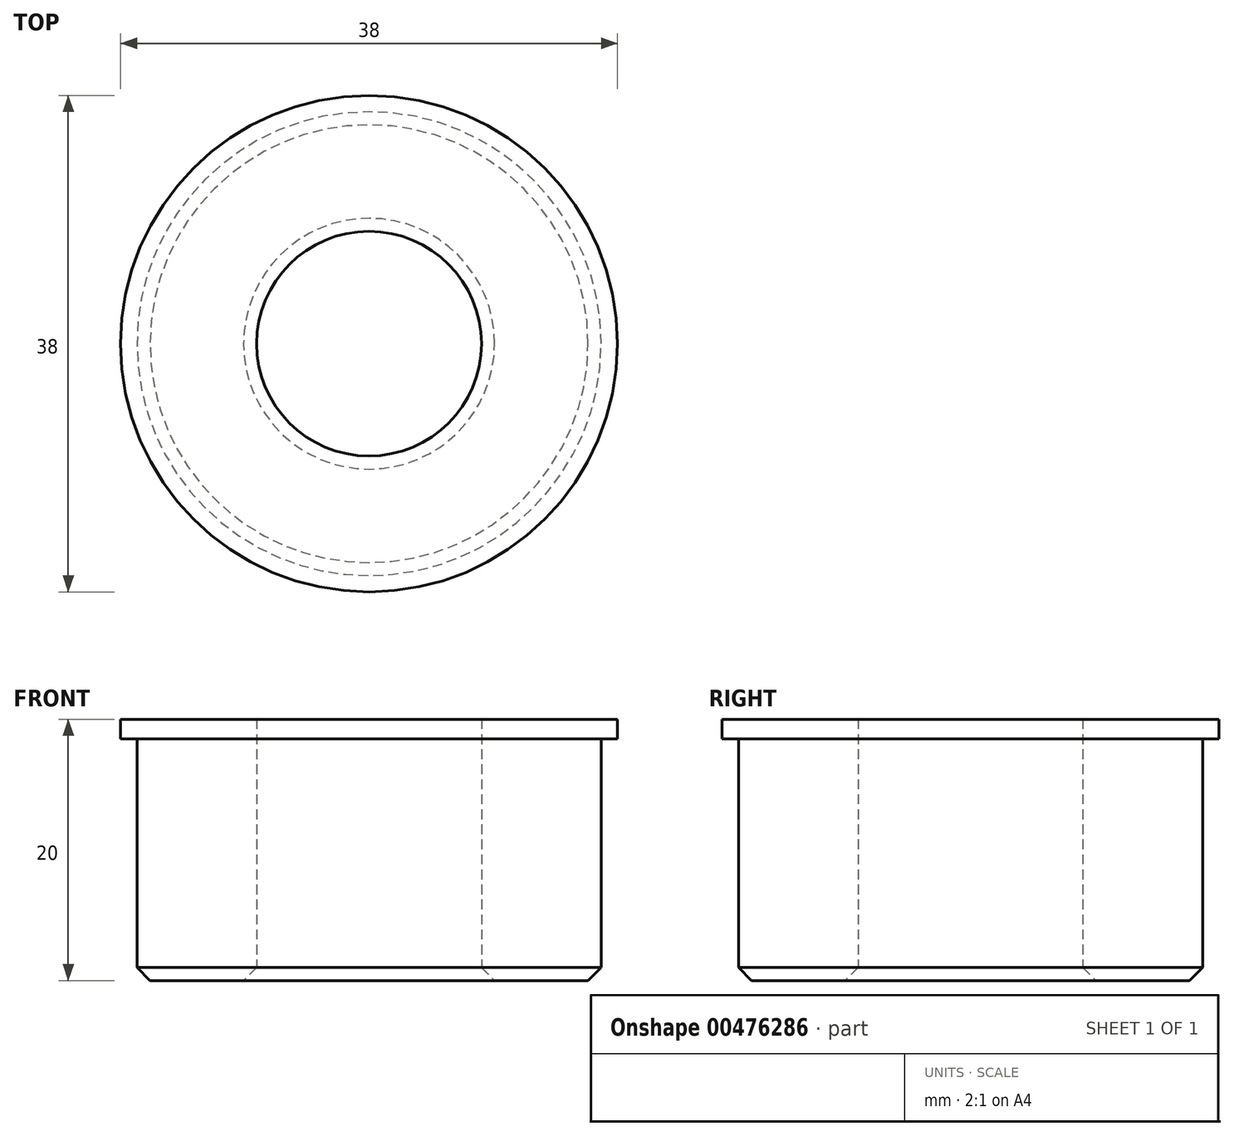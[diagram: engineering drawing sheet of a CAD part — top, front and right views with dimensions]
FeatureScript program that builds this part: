
annotation { "Feature Type Name" : "Feature", "Feature Type Description" : "" }
export const myFeature = defineFeature(function(context is Context, id is Id, definition is map)
    precondition{}
    {
        {
            var Q0;
            Q0=qCreatedBy(makeId("Top.planeOp"),FACE);
            var sketch = newSketch(context, id + "F0", { "sketchPlane" : qUnion([Q0])});
            skCircle(sketch, "E0", {"center": v(0, 0) * mm, "radius": 17.75 * mm});
            skCircle(sketch, "E1", {"center": v(0, 0) * mm, "radius": 8.6 * mm});
            skSolve(sketch);
        }
        {
            var Q0;
            Q0=makeQuery(id+"F0.imprint","IMPRINT",FACE,{"disambiguationData":[TD([[makeQuery(id+"F0.imprint","IMPRINT",EDGE,{"derivedFrom":sQuery(id+"F0.wireOp",EDGE,"E0")}),1.0]])]});
            extrude(context, id + "F1", {"entities" : qUnion([Q0]), "depth" : 20 * mm});
        }
        {
            var Q0;
            Q0=makeQuery(id+"F1.opExtrude","CAP_FACE",FACE,{"disambiguationData":[OSD([sQuery(id+"F0.wireOp",EDGE,"E0"),sQuery(id+"F0.wireOp",EDGE,"E1")])],"isStart":false});
            var sketch = newSketch(context, id + "F2", { "sketchPlane" : qUnion([Q0])});
            skCircle(sketch, "E2", {"center": v(0, 0) * mm, "radius": 19 * mm});
            skSolve(sketch);
        }
        {
            var Q0;
            Q0=makeQuery(id+"F2.imprint","IMPRINT",FACE,{"disambiguationData":[TD([[makeQuery(id+"F2.imprint","IMPRINT",EDGE,{"derivedFrom":sQuery(id+"F2.wireOp",EDGE,"E2")}),1.0]])]});
            extrude(context, id + "F3", {"entities" : qUnion([Q0]), "operationType" : NewBodyOperationType.ADD, "oppositeDirection" : true, "depth" : 1.5 * mm});
        }
        {
            var Q0;
            Q0=makeQuery(id+"F1.opExtrude","CAP_EDGE",EDGE,{"disambiguationData":[OSD([sQuery(id+"F0.wireOp",EDGE,"E0")])],"isStart":true});
            chamfer(context, id + "F4", {"entities" : qUnion([Q0]), "width" : 1 * mm, "tangentPropagation" : true});
        }
        {
            var Q0;
            Q0=makeQuery(id+"F1.opExtrude","CAP_EDGE",EDGE,{"disambiguationData":[OSD([sQuery(id+"F0.wireOp",EDGE,"E1")])],"isStart":true});
            chamfer(context, id + "F5", {"entities" : qUnion([Q0]), "width" : 1 * mm, "tangentPropagation" : true});
        }
    });
